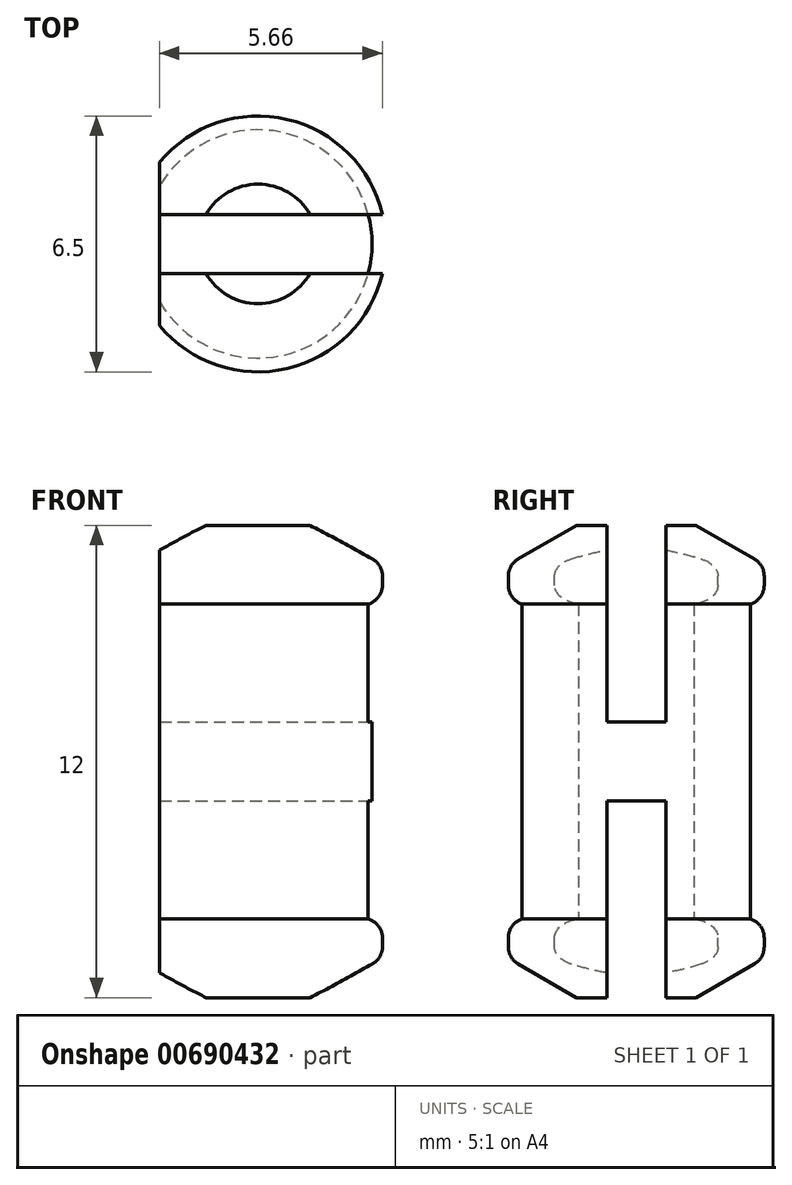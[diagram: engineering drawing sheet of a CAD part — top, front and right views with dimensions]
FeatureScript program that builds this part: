
annotation { "Feature Type Name" : "Feature", "Feature Type Description" : "" }
export const myFeature = defineFeature(function(context is Context, id is Id, definition is map)
    precondition{}
    {
        {
            var Q0;
            Q0=qCreatedBy(makeId("Top.planeOp"),FACE);
            var sketch = newSketch(context, id + "F0", { "sketchPlane" : qUnion([Q0])});
            skCircle(sketch, "E0", {"center": v(0, 0) * mm, "radius": 3.25 * mm});
            skSolve(sketch);
        }
        {
            var Q0;
            Q0 = qSketchRegion(id + "F0", true);
            extrude(context, id + "F1", {"entities" : qUnion([Q0]), "depth" : 2 * mm, "offsetDistance" : 25 * mm});
        }
        {
            var Q0;
            Q0=makeQuery(id+"F1.opExtrude","CAP_FACE",FACE,{"disambiguationData":[OSD([sQuery(id+"F0.wireOp",EDGE,"E0")])],"isStart":false});
            var sketch = newSketch(context, id + "F2", { "sketchPlane" : qUnion([Q0])});
            skCircle(sketch, "E1", {"center": v(0, 0) * mm, "radius": 2.9 * mm});
            skSolve(sketch);
        }
        {
            var Q0;
            Q0 = qSketchRegion(id + "F2", true);
            extrude(context, id + "F3", {"entities" : qUnion([Q0]), "operationType" : NewBodyOperationType.ADD, "depth" : 8 * mm, "offsetDistance" : 25 * mm});
        }
        {
            var Q0;
            Q0=makeQuery(id+"F3.opExtrude","CAP_FACE",FACE,{"disambiguationData":[OSD([sQuery(id+"F2.wireOp",EDGE,"E1")])],"isStart":false});
            var sketch = newSketch(context, id + "F4", { "sketchPlane" : qUnion([Q0])});
            skCircle(sketch, "E2", {"center": v(0, 0) * mm, "radius": 3.25 * mm});
            skSolve(sketch);
        }
        {
            var Q0;
            Q0 = qSketchRegion(id + "F4", true);
            extrude(context, id + "F5", {"entities" : qUnion([Q0]), "operationType" : NewBodyOperationType.ADD, "depth" : 2 * mm, "offsetDistance" : 25 * mm});
        }
        {
            var Q0;
            Q0=makeQuery(id+"F1.opExtrude","CAP_EDGE",EDGE,{"disambiguationData":[OSD([sQuery(id+"F0.wireOp",EDGE,"E0")])],"isStart":false});
            var Q1;
            Q1=makeQuery(id+"F5.opExtrude","CAP_EDGE",EDGE,{"disambiguationData":[OSD([sQuery(id+"F4.wireOp",EDGE,"E2")])],"isStart":true});
            fillet(context, id + "F6", {"entities" : qUnion([Q0, Q1]), "radius" : 0.5 * mm, "tangentPropagation" : true, "allowEdgeOverflow" : false});
        }
        {
            var Q0;
            Q0=makeQuery(id+"F1.opExtrude","CAP_FACE",FACE,{"disambiguationData":[OSD([sQuery(id+"F0.wireOp",EDGE,"E0")])],"isStart":true});
            var sketch = newSketch(context, id + "F7", { "sketchPlane" : qUnion([Q0])});
            skLineSegment(sketch, "E3", {"start": v(-3.16, -0.75) * mm, "end": v(3.16, -0.75) * mm});
            skLineSegment(sketch, "E4", {"start": v(3.16, 0.75) * mm, "end": v(-3.16, 0.75) * mm});
            skArc(sketch, "E5", {"start": v(-3.16, 0.75) * mm, "mid": v(-3.25, 0) * mm, "end": v(-3.16, -0.75) * mm});
            skArc(sketch, "E6", {"start": v(3.16, -0.75) * mm, "mid": v(3.25, 0) * mm, "end": v(3.16, 0.75) * mm});
            skSolve(sketch);
        }
        {
            var Q0;
            Q0 = qSketchRegion(id + "F7", true);
            extrude(context, id + "F8", {"entities" : qUnion([Q0]), "operationType" : NewBodyOperationType.REMOVE, "oppositeDirection" : true, "depth" : 5 * mm, "offsetDistance" : 25 * mm});
        }
        {
            var Q0;
            Q0=makeQuery(id+"F5.opExtrude","CAP_FACE",FACE,{"disambiguationData":[OSD([sQuery(id+"F4.wireOp",EDGE,"E2")])],"isStart":false});
            var sketch = newSketch(context, id + "F9", { "sketchPlane" : qUnion([Q0])});
            skLineSegment(sketch, "E7", {"start": v(-3.16, -0.75) * mm, "end": v(3.16, -0.75) * mm});
            skLineSegment(sketch, "E8", {"start": v(3.16, 0.75) * mm, "end": v(-3.16, 0.75) * mm});
            skArc(sketch, "E9", {"start": v(3.16, -0.75) * mm, "mid": v(3.25, 0) * mm, "end": v(3.16, 0.75) * mm});
            skArc(sketch, "E10", {"start": v(-3.16, 0.75) * mm, "mid": v(-3.25, 0) * mm, "end": v(-3.16, -0.75) * mm});
            skSolve(sketch);
        }
        {
            var Q0;
            Q0 = qSketchRegion(id + "F9", true);
            extrude(context, id + "F10", {"entities" : qUnion([Q0]), "operationType" : NewBodyOperationType.REMOVE, "oppositeDirection" : true, "depth" : 5 * mm, "offsetDistance" : 25 * mm});
        }
        {
            var Q0;
            {var subQ0=sQuery(id+"F0.wireOp",EDGE,"E0");Q0=makeQuery(id+"F8.boolean.opBoolean","SPLIT",EDGE,{"disambiguationData":[TD([makeQuery(id+"F8.opExtrude","SWEPT_FACE",FACE,{"disambiguationData":[OSD([sQuery(id+"F7.wireOp",EDGE,"E3")])]})])],"derivedFrom":makeQuery(id+"F1.opExtrude","CAP_EDGE",EDGE,{"disambiguationData":[OSD([subQ0])],"isStart":true})});}
            var Q1;
            {var subQ0=sQuery(id+"F0.wireOp",EDGE,"E0");Q1=makeQuery(id+"F8.boolean.opBoolean","SPLIT",EDGE,{"disambiguationData":[TD([makeQuery(id+"F8.opExtrude","SWEPT_FACE",FACE,{"disambiguationData":[OSD([sQuery(id+"F7.wireOp",EDGE,"E4")])]})])],"derivedFrom":makeQuery(id+"F1.opExtrude","CAP_EDGE",EDGE,{"disambiguationData":[OSD([subQ0])],"isStart":true})});}
            chamfer(context, id + "F11", {"entities" : qUnion([Q0, Q1]), "chamferType" : ChamferType.OFFSET_ANGLE, "width" : 1 * mm, "oppositeDirection" : false, "angle" : 60 * degree, "tangentPropagation" : true});
        }
        {
            var Q0;
            {var subQ0=sQuery(id+"F4.wireOp",EDGE,"E2");Q0=makeQuery(id+"F10.boolean.opBoolean","SPLIT",EDGE,{"disambiguationData":[TD([makeQuery(id+"F10.opExtrude","SWEPT_FACE",FACE,{"disambiguationData":[OSD([sQuery(id+"F9.wireOp",EDGE,"E7")])]})])],"derivedFrom":makeQuery(id+"F5.opExtrude","CAP_EDGE",EDGE,{"disambiguationData":[OSD([subQ0])],"isStart":false})});}
            var Q1;
            {var subQ0=sQuery(id+"F4.wireOp",EDGE,"E2");Q1=makeQuery(id+"F10.boolean.opBoolean","SPLIT",EDGE,{"disambiguationData":[TD([makeQuery(id+"F10.opExtrude","SWEPT_FACE",FACE,{"disambiguationData":[OSD([sQuery(id+"F9.wireOp",EDGE,"E8")])]})])],"derivedFrom":makeQuery(id+"F5.opExtrude","CAP_EDGE",EDGE,{"disambiguationData":[OSD([subQ0])],"isStart":false})});}
            chamfer(context, id + "F12", {"entities" : qUnion([Q0, Q1]), "chamferType" : ChamferType.OFFSET_ANGLE, "width" : 1 * mm, "oppositeDirection" : true, "angle" : 60 * degree, "tangentPropagation" : true});
        }
        {
            var Q0;
            {var subQ0=sQuery(id+"F4.wireOp",EDGE,"E2");var subQ2=makeQuery(id+"F10.opExtrude","SWEPT_FACE",FACE,{"disambiguationData":[OSD([sQuery(id+"F9.wireOp",EDGE,"E7")])]});var subQ3=makeQuery(id+"F5.opExtrude","SWEPT_FACE",FACE,{"disambiguationData":[OSD([subQ0])]});Q0=makeQuery(id+"F12.opChamfer","BLEND_EDGE",EDGE,{"blendedFrom":[makeQuery(id+"F10.boolean.opBoolean","SPLIT",EDGE,{"disambiguationData":[TD([subQ2])],"derivedFrom":makeQuery(id+"F5.opExtrude","CAP_EDGE",EDGE,{"disambiguationData":[OSD([subQ0])],"isStart":false})}),makeQuery(id+"F10.boolean.opBoolean","SPLIT",FACE,{"disambiguationData":[TD([subQ2])],"derivedFrom":subQ3})],"blendedInto":[makeQuery(id+"F10.boolean.opBoolean","SPLIT",FACE,{"disambiguationData":[TD([subQ2])],"derivedFrom":subQ3})]});}
            var Q1;
            {var subQ0=sQuery(id+"F4.wireOp",EDGE,"E2");var subQ2=makeQuery(id+"F10.opExtrude","SWEPT_FACE",FACE,{"disambiguationData":[OSD([sQuery(id+"F9.wireOp",EDGE,"E8")])]});var subQ3=makeQuery(id+"F5.opExtrude","SWEPT_FACE",FACE,{"disambiguationData":[OSD([subQ0])]});Q1=makeQuery(id+"F12.opChamfer","BLEND_EDGE",EDGE,{"blendedFrom":[makeQuery(id+"F10.boolean.opBoolean","SPLIT",EDGE,{"disambiguationData":[TD([subQ2])],"derivedFrom":makeQuery(id+"F5.opExtrude","CAP_EDGE",EDGE,{"disambiguationData":[OSD([subQ0])],"isStart":false})}),makeQuery(id+"F10.boolean.opBoolean","SPLIT",FACE,{"disambiguationData":[TD([subQ2])],"derivedFrom":subQ3})],"blendedInto":[makeQuery(id+"F10.boolean.opBoolean","SPLIT",FACE,{"disambiguationData":[TD([subQ2])],"derivedFrom":subQ3})]});}
            var Q2;
            {var subQ0=sQuery(id+"F0.wireOp",EDGE,"E0");var subQ2=makeQuery(id+"F8.opExtrude","SWEPT_FACE",FACE,{"disambiguationData":[OSD([sQuery(id+"F7.wireOp",EDGE,"E4")])]});var subQ3=makeQuery(id+"F1.opExtrude","SWEPT_FACE",FACE,{"disambiguationData":[OSD([subQ0])]});Q2=makeQuery(id+"F11.opChamfer","BLEND_EDGE",EDGE,{"blendedFrom":[makeQuery(id+"F8.boolean.opBoolean","SPLIT",EDGE,{"disambiguationData":[TD([subQ2])],"derivedFrom":makeQuery(id+"F1.opExtrude","CAP_EDGE",EDGE,{"disambiguationData":[OSD([subQ0])],"isStart":true})}),makeQuery(id+"F8.boolean.opBoolean","SPLIT",FACE,{"disambiguationData":[TD([subQ2])],"derivedFrom":subQ3})],"blendedInto":[makeQuery(id+"F8.boolean.opBoolean","SPLIT",FACE,{"disambiguationData":[TD([subQ2])],"derivedFrom":subQ3})]});}
            var Q3;
            {var subQ0=sQuery(id+"F0.wireOp",EDGE,"E0");var subQ2=makeQuery(id+"F8.opExtrude","SWEPT_FACE",FACE,{"disambiguationData":[OSD([sQuery(id+"F7.wireOp",EDGE,"E3")])]});var subQ3=makeQuery(id+"F1.opExtrude","SWEPT_FACE",FACE,{"disambiguationData":[OSD([subQ0])]});Q3=makeQuery(id+"F11.opChamfer","BLEND_EDGE",EDGE,{"blendedFrom":[makeQuery(id+"F8.boolean.opBoolean","SPLIT",EDGE,{"disambiguationData":[TD([subQ2])],"derivedFrom":makeQuery(id+"F1.opExtrude","CAP_EDGE",EDGE,{"disambiguationData":[OSD([subQ0])],"isStart":true})}),makeQuery(id+"F8.boolean.opBoolean","SPLIT",FACE,{"disambiguationData":[TD([subQ2])],"derivedFrom":subQ3})],"blendedInto":[makeQuery(id+"F8.boolean.opBoolean","SPLIT",FACE,{"disambiguationData":[TD([subQ2])],"derivedFrom":subQ3})]});}
            fillet(context, id + "F13", {"entities" : qUnion([Q0, Q1, Q2, Q3]), "radius" : 0.5 * mm, "tangentPropagation" : true, "allowEdgeOverflow" : false});
        }
        {
            var Q0;
            {var subQ0=sQuery(id+"F4.wireOp",EDGE,"E2");Q0=makeQuery(id+"F10.boolean.opBoolean","SPLIT",FACE,{"disambiguationData":[TD([makeQuery(id+"F10.opExtrude","SWEPT_FACE",FACE,{"disambiguationData":[OSD([sQuery(id+"F9.wireOp",EDGE,"E8")])]})])],"derivedFrom":makeQuery(id+"F5.opExtrude","CAP_FACE",FACE,{"disambiguationData":[OSD([subQ0])],"isStart":false})});}
            var sketch = newSketch(context, id + "F14", { "sketchPlane" : qUnion([Q0])});
            skArc(sketch, "E11", {"start": v(-2.5, 2.08) * mm, "mid": v(-3.25, 0) * mm, "end": v(-2.5, -2.08) * mm});
            skLineSegment(sketch, "E12", {"start": v(-2.5, -2.08) * mm, "end": v(-2.5, 2.08) * mm});
            skSolve(sketch);
        }
        {
            var Q0;
            Q0 = qSketchRegion(id + "F14", true);
            extrude(context, id + "F15", {"entities" : qUnion([Q0]), "operationType" : NewBodyOperationType.REMOVE, "oppositeDirection" : true, "depth" : 25 * mm, "offsetDistance" : 25 * mm});
        }
    });
